# Revit family: IS_Mara_A5688_BIM_FR
name_source: partatom
category: Plumbing Fixtures
revit_build: Autodesk Revit 2017 (Build: 20160225_1515(x64)
units: mm (PartAtom-declared; Revit-internal decimal feet)

## family parameters
Always vertical = No
Cut with Voids When Loaded = No
OmniClass Number = 23.45.55.17
OmniClass Title = Mixing Faucets
Part Type = Normal
Room Calculation Point = No
Round Connector Dimension = Use Diameter
Shared = No
Work Plane-Based = No

## types (1)
- A5688 - Colonne Mitigeur
    Accessoires = www.idealstandard.be
    Assembly Code = C1030200
    Auteur = Ideal Standard
    BOSUseNativeGeometries = 1
    Caractéristiques = Colonne Mitigeur
    CodeBarre = 4015413314657
    ConseilsDInstallation = www.idealstandard.be
    Couleur = chromé
    CoûtDeRemplacement = 0
    DateDeCréation = 2018_08_15
    Description = Colonne Mitigeur
    Dimensions = 1444 x 483 x 464
    DuréeDeGarantieDesPièces = 5
    DuréeGarantie = year
    DébitL/Mn = Litres
    DétailGarantie = Manufacturers Warranty
    Espace = Internal
    Finition = chromé
    Forme = Rectangular
    Hauteur = 1444 mm
    IfcExportAs = IfcSanitaryTerminalType
    IfcExportType = SHOWER
    InformationsProduit = www.idealstandard.be
    Largeur = 483 mm
    LienUtile = www.idealstandard.be
    Longueur = 463 mm
    Manufacturer = www.idealstandard.be
    Marque = Ideal Standard
    Matériel = Laiton
    Model = A5688
    Nom = Colonne Mitigeur
    PoidsBrut = 7.025
    PoidsNet = 7.025
    PressionDeFonctionnement = 0
    Révision = 1
    URL = www.idealstandard.be
    UrlDuFabricant = www.idealstandard.be

## geometry (parser evidence)
native form markers: Sweep x2
no freeform markers — native parametric forms only
